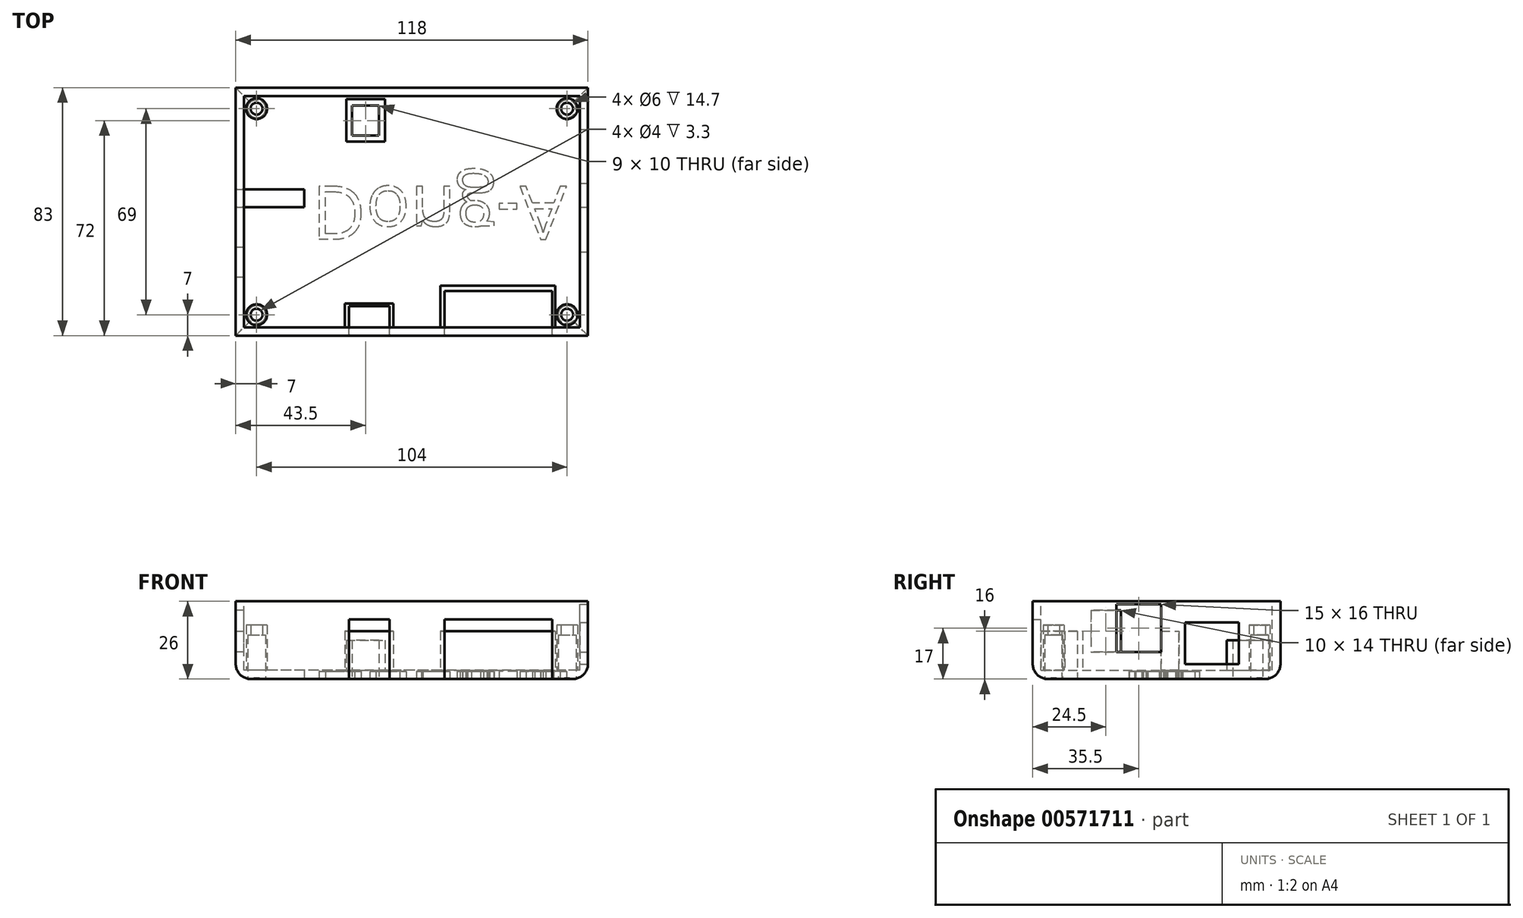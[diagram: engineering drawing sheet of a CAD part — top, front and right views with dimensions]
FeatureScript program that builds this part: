
annotation { "Feature Type Name" : "Feature", "Feature Type Description" : "" }
export const myFeature = defineFeature(function(context is Context, id is Id, definition is map)
    precondition{}
    {
        {
            var Q0;
            Q0=qCreatedBy(makeId("Top.planeOp"),FACE);
            var sketch = newSketch(context, id + "F0", { "sketchPlane" : qUnion([Q0])});
            skLineSegment(sketch, "E0.bottom", {"start": v(59, -41.5) * mm, "end": v(-59, -41.5) * mm});
            skLineSegment(sketch, "E0.top", {"start": v(59, 41.5) * mm, "end": v(-59, 41.5) * mm});
            skLineSegment(sketch, "E0.left", {"start": v(59, -41.5) * mm, "end": v(59, 41.5) * mm});
            skLineSegment(sketch, "E0.right", {"start": v(-59, -41.5) * mm, "end": v(-59, 41.5) * mm});
            skPoint(sketch, "E0.middle", {"position": v(0, 0) * mm});
            skSolve(sketch);
        }
        {
            var Q0;
            Q0=makeQuery(id+"F0.imprint","IMPRINT",FACE,{"disambiguationData":[TD([[makeQuery(id+"F0.imprint","IMPRINT",EDGE,{"derivedFrom":sQuery(id+"F0.wireOp",EDGE,"E0.bottom")}),-1.0]])]});
            extrude(context, id + "F1", {"entities" : qUnion([Q0]), "depth" : 26 * mm, "offsetDistance" : 25.4 * mm});
        }
        {
            var Q0;
            Q0=makeQuery(id+"F1.opExtrude","CAP_FACE",FACE,{"disambiguationData":[OSD([sQuery(id+"F0.wireOp",EDGE,"E0.bottom"),sQuery(id+"F0.wireOp",EDGE,"E0.top"),sQuery(id+"F0.wireOp",EDGE,"E0.left"),sQuery(id+"F0.wireOp",EDGE,"E0.right")])],"isStart":false});
            var sketch = newSketch(context, id + "F2", { "sketchPlane" : qUnion([Q0])});
            skLineSegment(sketch, "E1.bottom", {"start": v(56.25, -38.75) * mm, "end": v(-56.25, -38.75) * mm});
            skLineSegment(sketch, "E1.top", {"start": v(56.25, 38.75) * mm, "end": v(-56.25, 38.75) * mm});
            skLineSegment(sketch, "E1.left", {"start": v(56.25, -38.75) * mm, "end": v(56.25, 38.75) * mm});
            skLineSegment(sketch, "E1.right", {"start": v(-56.25, -38.75) * mm, "end": v(-56.25, 38.75) * mm});
            skPoint(sketch, "E1.middle", {"position": v(0, 0) * mm});
            skSolve(sketch);
        }
        {
            var Q0;
            Q0 = qSketchRegion(id + "F2", true);
            extrude(context, id + "F3", {"entities" : qUnion([Q0]), "operationType" : NewBodyOperationType.REMOVE, "oppositeDirection" : true, "depth" : 23 * mm, "offsetDistance" : 25.4 * mm});
        }
        {
            var Q0;
            Q0=makeQuery(id+"F1.opExtrude","CAP_FACE",FACE,{"disambiguationData":[OSD([sQuery(id+"F0.wireOp",EDGE,"E0.bottom"),sQuery(id+"F0.wireOp",EDGE,"E0.top"),sQuery(id+"F0.wireOp",EDGE,"E0.left"),sQuery(id+"F0.wireOp",EDGE,"E0.right")])],"isStart":true});
            var sketch = newSketch(context, id + "F4", { "sketchPlane" : qUnion([Q0])});
            skLineSegment(sketch, "E2.bottom", {"start": v(47, 41.5) * mm, "end": v(11, 41.5) * mm});
            skLineSegment(sketch, "E2.top", {"start": v(47, 26.5) * mm, "end": v(11, 26.5) * mm});
            skLineSegment(sketch, "E2.left", {"start": v(47, 41.5) * mm, "end": v(47, 26.5) * mm});
            skLineSegment(sketch, "E2.right", {"start": v(11, 41.5) * mm, "end": v(11, 26.5) * mm});
            skLineSegment(sketch, "E3.bottom", {"start": v(-7.5, 41.5) * mm, "end": v(-21, 41.5) * mm});
            skLineSegment(sketch, "E3.top", {"start": v(-7.5, 31.7) * mm, "end": v(-21, 31.7) * mm});
            skLineSegment(sketch, "E3.left", {"start": v(-7.5, 41.5) * mm, "end": v(-7.5, 31.7) * mm});
            skLineSegment(sketch, "E3.right", {"start": v(-21, 41.5) * mm, "end": v(-21, 31.7) * mm});
            skSolve(sketch);
        }
        {
            var Q0;
            Q0 = qSketchRegion(id + "F4", true);
            extrude(context, id + "F5", {"entities" : qUnion([Q0]), "operationType" : NewBodyOperationType.REMOVE, "oppositeDirection" : true, "depth" : 20 * mm, "offsetDistance" : 25.4 * mm});
        }
        {
            var Q0;
            Q0=makeQuery(id+"F3.boolean.opBoolean","COPY",FACE,{"derivedFrom":makeQuery(id+"F3.opExtrude","CAP_FACE",FACE,{"disambiguationData":[OSD([sQuery(id+"F2.wireOp",EDGE,"E1.bottom"),sQuery(id+"F2.wireOp",EDGE,"E1.top"),sQuery(id+"F2.wireOp",EDGE,"E1.left"),sQuery(id+"F2.wireOp",EDGE,"E1.right")])],"isStart":false})});
            var sketch = newSketch(context, id + "F6", { "sketchPlane" : qUnion([Q0])});
            skLineSegment(sketch, "E4.bottom", {"start": v(47, -38.75) * mm, "end": v(48, -38.75) * mm});
            skLineSegment(sketch, "E4.top", {"start": v(47, -24.75) * mm, "end": v(48, -24.75) * mm});
            skLineSegment(sketch, "E4.left", {"start": v(47, -38.75) * mm, "end": v(47, -24.75) * mm});
            skLineSegment(sketch, "E4.right", {"start": v(48, -38.75) * mm, "end": v(48, -24.75) * mm});
            skLineSegment(sketch, "E5.bottom", {"start": v(11, -38.75) * mm, "end": v(9.5, -38.75) * mm});
            skLineSegment(sketch, "E5.top", {"start": v(11, -24.75) * mm, "end": v(9.5, -24.75) * mm});
            skLineSegment(sketch, "E5.left", {"start": v(11, -38.75) * mm, "end": v(11, -24.75) * mm});
            skLineSegment(sketch, "E5.right", {"start": v(9.5, -38.75) * mm, "end": v(9.5, -24.75) * mm});
            skLineSegment(sketch, "E6.bottom", {"start": v(47, -24.75) * mm, "end": v(11, -24.75) * mm});
            skLineSegment(sketch, "E6.top", {"start": v(47, -26.5) * mm, "end": v(11, -26.5) * mm});
            skLineSegment(sketch, "E6.left", {"start": v(47, -24.75) * mm, "end": v(47, -26.5) * mm});
            skLineSegment(sketch, "E6.right", {"start": v(11, -24.75) * mm, "end": v(11, -26.5) * mm});
            skLineSegment(sketch, "E7.bottom", {"start": v(-7.5, -38.75) * mm, "end": v(-6.2, -38.75) * mm});
            skLineSegment(sketch, "E7.top", {"start": v(-7.5, -30.75) * mm, "end": v(-6.2, -30.75) * mm});
            skLineSegment(sketch, "E7.left", {"start": v(-7.5, -38.75) * mm, "end": v(-7.5, -30.75) * mm});
            skLineSegment(sketch, "E7.right", {"start": v(-6.2, -38.75) * mm, "end": v(-6.2, -30.75) * mm});
            skLineSegment(sketch, "E8.bottom", {"start": v(-21, -38.75) * mm, "end": v(-22.5, -38.75) * mm});
            skLineSegment(sketch, "E8.top", {"start": v(-21, -30.75) * mm, "end": v(-22.5, -30.75) * mm});
            skLineSegment(sketch, "E8.left", {"start": v(-21, -38.75) * mm, "end": v(-21, -30.75) * mm});
            skLineSegment(sketch, "E8.right", {"start": v(-22.5, -38.75) * mm, "end": v(-22.5, -30.75) * mm});
            skLineSegment(sketch, "E9.bottom", {"start": v(-7.5, -30.75) * mm, "end": v(-21, -30.75) * mm});
            skLineSegment(sketch, "E9.top", {"start": v(-7.5, -31.7) * mm, "end": v(-21, -31.7) * mm});
            skLineSegment(sketch, "E9.left", {"start": v(-7.5, -30.75) * mm, "end": v(-7.5, -31.7) * mm});
            skLineSegment(sketch, "E9.right", {"start": v(-21, -30.75) * mm, "end": v(-21, -31.7) * mm});
            skSolve(sketch);
        }
        {
            var Q0;
            Q0 = qSketchRegion(id + "F6", true);
            extrude(context, id + "F7", {"entities" : qUnion([Q0]), "operationType" : NewBodyOperationType.ADD, "depth" : 13 * mm, "offsetDistance" : 25.4 * mm});
        }
        {
            var Q0;
            Q0=makeQuery(id+"F1.opExtrude","SWEPT_FACE",FACE,{"disambiguationData":[OSD([sQuery(id+"F0.wireOp",EDGE,"E0.right")])]});
            var sketch = newSketch(context, id + "F8", { "sketchPlane" : qUnion([Q0])});
            skLineSegment(sketch, "E10.bottom", {"start": v(22, 23) * mm, "end": v(12, 23) * mm});
            skLineSegment(sketch, "E10.top", {"start": v(22, 9) * mm, "end": v(12, 9) * mm});
            skLineSegment(sketch, "E10.left", {"start": v(22, 23) * mm, "end": v(22, 9) * mm});
            skLineSegment(sketch, "E10.right", {"start": v(12, 23) * mm, "end": v(12, 9) * mm});
            skSolve(sketch);
        }
        {
            var Q0;
            Q0 = qSketchRegion(id + "F8", true);
            extrude(context, id + "F9", {"entities" : qUnion([Q0]), "operationType" : NewBodyOperationType.REMOVE, "oppositeDirection" : true, "depth" : 10 * mm, "offsetDistance" : 25.4 * mm});
        }
        {
            var Q0;
            Q0=makeQuery(id+"F1.opExtrude","CAP_FACE",FACE,{"disambiguationData":[OSD([sQuery(id+"F0.wireOp",EDGE,"E0.bottom"),sQuery(id+"F0.wireOp",EDGE,"E0.top"),sQuery(id+"F0.wireOp",EDGE,"E0.left"),sQuery(id+"F0.wireOp",EDGE,"E0.right")])],"isStart":true});
            var sketch = newSketch(context, id + "F10", { "sketchPlane" : qUnion([Q0])});
            skLineSegment(sketch, "E11.bottom", {"start": v(-59, -1.5) * mm, "end": v(-36, -1.5) * mm});
            skLineSegment(sketch, "E11.top", {"start": v(-59, -7.5) * mm, "end": v(-36, -7.5) * mm});
            skLineSegment(sketch, "E11.left", {"start": v(-59, -1.5) * mm, "end": v(-59, -7.5) * mm});
            skLineSegment(sketch, "E11.right", {"start": v(-36, -1.5) * mm, "end": v(-36, -7.5) * mm});
            skSolve(sketch);
        }
        {
            var Q0;
            Q0 = qSketchRegion(id + "F10", true);
            extrude(context, id + "F11", {"entities" : qUnion([Q0]), "operationType" : NewBodyOperationType.REMOVE, "oppositeDirection" : true, "depth" : 16 * mm, "offsetDistance" : 25.4 * mm});
        }
        {
            var Q0;
            Q0=makeQuery(id+"F1.opExtrude","CAP_FACE",FACE,{"disambiguationData":[OSD([sQuery(id+"F0.wireOp",EDGE,"E0.bottom"),sQuery(id+"F0.wireOp",EDGE,"E0.top"),sQuery(id+"F0.wireOp",EDGE,"E0.left"),sQuery(id+"F0.wireOp",EDGE,"E0.right")])],"isStart":true});
            var sketch = newSketch(context, id + "F12", { "sketchPlane" : qUnion([Q0])});
            skLineSegment(sketch, "E12.bottom", {"start": v(-20, -35.5) * mm, "end": v(-11, -35.5) * mm});
            skLineSegment(sketch, "E12.top", {"start": v(-20, -25.5) * mm, "end": v(-11, -25.5) * mm});
            skLineSegment(sketch, "E12.left", {"start": v(-20, -35.5) * mm, "end": v(-20, -25.5) * mm});
            skLineSegment(sketch, "E12.right", {"start": v(-11, -35.5) * mm, "end": v(-11, -25.5) * mm});
            skSolve(sketch);
        }
        {
            var Q0;
            Q0 = qSketchRegion(id + "F12", true);
            extrude(context, id + "F13", {"entities" : qUnion([Q0]), "operationType" : NewBodyOperationType.REMOVE, "oppositeDirection" : true, "depth" : 10 * mm, "offsetDistance" : 25.4 * mm});
        }
        {
            var Q0;
            Q0=makeQuery(id+"F1.opExtrude","SWEPT_FACE",FACE,{"disambiguationData":[OSD([sQuery(id+"F0.wireOp",EDGE,"E0.left")])]});
            var sketch = newSketch(context, id + "F14", { "sketchPlane" : qUnion([Q0])});
            skLineSegment(sketch, "E13.bottom", {"start": v(27.5, 19) * mm, "end": v(9.5, 19) * mm});
            skLineSegment(sketch, "E13.top", {"start": v(27.5, 5) * mm, "end": v(9.5, 5) * mm});
            skLineSegment(sketch, "E13.left", {"start": v(27.5, 19) * mm, "end": v(27.5, 5) * mm});
            skLineSegment(sketch, "E13.right", {"start": v(9.5, 19) * mm, "end": v(9.5, 5) * mm});
            skLineSegment(sketch, "E14.bottom", {"start": v(-13.5, 9) * mm, "end": v(1.5, 9) * mm});
            skLineSegment(sketch, "E14.top", {"start": v(-13.5, 25) * mm, "end": v(1.5, 25) * mm});
            skLineSegment(sketch, "E14.left", {"start": v(-13.5, 9) * mm, "end": v(-13.5, 25) * mm});
            skLineSegment(sketch, "E14.right", {"start": v(1.5, 9) * mm, "end": v(1.5, 25) * mm});
            skSolve(sketch);
        }
        {
            var Q0;
            Q0 = qSketchRegion(id + "F14", true);
            extrude(context, id + "F15", {"entities" : qUnion([Q0]), "operationType" : NewBodyOperationType.REMOVE, "oppositeDirection" : true, "depth" : 10 * mm, "offsetDistance" : 25.4 * mm});
        }
        {
            var Q0;
            Q0=makeQuery(id+"F3.boolean.opBoolean","COPY",FACE,{"derivedFrom":makeQuery(id+"F3.opExtrude","CAP_FACE",FACE,{"disambiguationData":[OSD([sQuery(id+"F2.wireOp",EDGE,"E1.bottom"),sQuery(id+"F2.wireOp",EDGE,"E1.top"),sQuery(id+"F2.wireOp",EDGE,"E1.left"),sQuery(id+"F2.wireOp",EDGE,"E1.right")])],"isStart":false})});
            var sketch = newSketch(context, id + "F16", { "sketchPlane" : qUnion([Q0])});
            skLineSegment(sketch, "E15.bottom", {"start": v(-22, 25.5) * mm, "end": v(-11, 25.5) * mm});
            skLineSegment(sketch, "E15.top", {"start": v(-22, 23.5) * mm, "end": v(-11, 23.5) * mm});
            skLineSegment(sketch, "E15.left", {"start": v(-22, 25.5) * mm, "end": v(-22, 23.5) * mm});
            skLineSegment(sketch, "E15.right", {"start": v(-11, 25.5) * mm, "end": v(-11, 23.5) * mm});
            skLineSegment(sketch, "E16.bottom", {"start": v(-11, 23.5) * mm, "end": v(-9, 23.5) * mm});
            skLineSegment(sketch, "E16.top", {"start": v(-11, 37.68) * mm, "end": v(-9, 37.68) * mm});
            skLineSegment(sketch, "E16.left", {"start": v(-11, 23.5) * mm, "end": v(-11, 37.68) * mm});
            skLineSegment(sketch, "E16.right", {"start": v(-9, 23.5) * mm, "end": v(-9, 37.68) * mm});
            skLineSegment(sketch, "E17.bottom", {"start": v(-22, 25.5) * mm, "end": v(-20, 25.5) * mm});
            skLineSegment(sketch, "E17.top", {"start": v(-22, 37.68) * mm, "end": v(-20, 37.68) * mm});
            skLineSegment(sketch, "E17.left", {"start": v(-22, 25.5) * mm, "end": v(-22, 37.68) * mm});
            skLineSegment(sketch, "E17.right", {"start": v(-20, 25.5) * mm, "end": v(-20, 37.68) * mm});
            skLineSegment(sketch, "E18.bottom", {"start": v(-20, 37.68) * mm, "end": v(-11, 37.68) * mm});
            skLineSegment(sketch, "E18.top", {"start": v(-20, 35.5) * mm, "end": v(-11, 35.5) * mm});
            skLineSegment(sketch, "E18.left", {"start": v(-20, 37.68) * mm, "end": v(-20, 35.5) * mm});
            skLineSegment(sketch, "E18.right", {"start": v(-11, 37.68) * mm, "end": v(-11, 35.5) * mm});
            skSolve(sketch);
        }
        {
            var Q0;
            Q0 = qSketchRegion(id + "F16", true);
            extrude(context, id + "F17", {"entities" : qUnion([Q0]), "operationType" : NewBodyOperationType.ADD, "depth" : 10 * mm, "offsetDistance" : 25.4 * mm});
        }
        {
            var Q0;
            Q0=makeQuery(id+"F1.opExtrude","CAP_FACE",FACE,{"disambiguationData":[OSD([sQuery(id+"F0.wireOp",EDGE,"E0.bottom"),sQuery(id+"F0.wireOp",EDGE,"E0.top"),sQuery(id+"F0.wireOp",EDGE,"E0.left"),sQuery(id+"F0.wireOp",EDGE,"E0.right")])],"isStart":true});
            var sketch = newSketch(context, id + "F18", { "sketchPlane" : qUnion([Q0])});
            skCircle(sketch, "E19", {"center": v(-52, -34.5) * mm, "radius": 3 * mm});
            skCircle(sketch, "E20", {"center": v(-52, 34.5) * mm, "radius": 3 * mm});
            skCircle(sketch, "E21", {"center": v(52, -34.5) * mm, "radius": 3 * mm});
            skCircle(sketch, "E22", {"center": v(52, 34.5) * mm, "radius": 3 * mm});
            skSolve(sketch);
        }
        {
            var Q0;
            Q0 = qSketchRegion(id + "F18", true);
            extrude(context, id + "F19", {"entities" : qUnion([Q0]), "operationType" : NewBodyOperationType.REMOVE, "oppositeDirection" : true, "depth" : 25.4 * mm, "offsetDistance" : 25.4 * mm});
        }
        {
            var Q0;
            {var subQ0=sQuery(id+"F2.wireOp",EDGE,"E1.bottom");var subQ1=sQuery(id+"F2.wireOp",EDGE,"E1.top");var subQ2=sQuery(id+"F2.wireOp",EDGE,"E1.left");var subQ3=sQuery(id+"F2.wireOp",EDGE,"E1.right");Q0=makeQuery(id+"F19.boolean.opBoolean","SPLIT",FACE,{"disambiguationData":[TD([makeQuery(id+"F3.boolean.opBoolean","COPY",FACE,{"derivedFrom":makeQuery(id+"F3.opExtrude","SWEPT_FACE",FACE,{"disambiguationData":[OSD([subQ0])]})}),makeQuery(id+"F3.boolean.opBoolean","COPY",FACE,{"derivedFrom":makeQuery(id+"F3.opExtrude","SWEPT_FACE",FACE,{"disambiguationData":[OSD([subQ1])]})}),makeQuery(id+"F3.boolean.opBoolean","COPY",FACE,{"derivedFrom":makeQuery(id+"F3.opExtrude","SWEPT_FACE",FACE,{"disambiguationData":[OSD([subQ2])]})}),makeQuery(id+"F3.boolean.opBoolean","COPY",FACE,{"derivedFrom":makeQuery(id+"F3.opExtrude","SWEPT_FACE",FACE,{"disambiguationData":[OSD([subQ3])]})}),makeQuery(id+"F7.opExtrude","SWEPT_FACE",FACE,{"disambiguationData":[OSD([sQuery(id+"F6.wireOp",EDGE,"E4.top"),sQuery(id+"F6.wireOp",EDGE,"E5.top"),sQuery(id+"F6.wireOp",EDGE,"E6.bottom")])]}),makeQuery(id+"F7.opExtrude","SWEPT_FACE",FACE,{"disambiguationData":[OSD([sQuery(id+"F6.wireOp",EDGE,"E4.right")])]}),makeQuery(id+"F7.opExtrude","SWEPT_FACE",FACE,{"disambiguationData":[OSD([sQuery(id+"F6.wireOp",EDGE,"E5.right")])]}),makeQuery(id+"F7.opExtrude","SWEPT_FACE",FACE,{"disambiguationData":[OSD([sQuery(id+"F6.wireOp",EDGE,"E7.top"),sQuery(id+"F6.wireOp",EDGE,"E8.top"),sQuery(id+"F6.wireOp",EDGE,"E9.bottom")])]}),makeQuery(id+"F7.opExtrude","SWEPT_FACE",FACE,{"disambiguationData":[OSD([sQuery(id+"F6.wireOp",EDGE,"E7.right")])]}),makeQuery(id+"F7.opExtrude","SWEPT_FACE",FACE,{"disambiguationData":[OSD([sQuery(id+"F6.wireOp",EDGE,"E8.right")])]}),makeQuery(id+"F11.boolean.opBoolean","COPY",FACE,{"derivedFrom":makeQuery(id+"F11.opExtrude","SWEPT_FACE",FACE,{"disambiguationData":[OSD([sQuery(id+"F10.wireOp",EDGE,"E11.bottom")])]})}),makeQuery(id+"F11.boolean.opBoolean","COPY",FACE,{"derivedFrom":makeQuery(id+"F11.opExtrude","SWEPT_FACE",FACE,{"disambiguationData":[OSD([sQuery(id+"F10.wireOp",EDGE,"E11.top")])]})}),makeQuery(id+"F11.boolean.opBoolean","COPY",FACE,{"derivedFrom":makeQuery(id+"F11.opExtrude","SWEPT_FACE",FACE,{"disambiguationData":[OSD([sQuery(id+"F10.wireOp",EDGE,"E11.right")])]})}),makeQuery(id+"F17.opExtrude","SWEPT_FACE",FACE,{"disambiguationData":[OSD([sQuery(id+"F16.wireOp",EDGE,"E15.top"),sQuery(id+"F16.wireOp",EDGE,"E16.bottom")])]}),makeQuery(id+"F17.opExtrude","SWEPT_FACE",FACE,{"disambiguationData":[OSD([sQuery(id+"F16.wireOp",EDGE,"E15.left"),sQuery(id+"F16.wireOp",EDGE,"E17.left")])]}),makeQuery(id+"F17.opExtrude","SWEPT_FACE",FACE,{"disambiguationData":[OSD([sQuery(id+"F16.wireOp",EDGE,"E16.top"),sQuery(id+"F16.wireOp",EDGE,"E17.top"),sQuery(id+"F16.wireOp",EDGE,"E18.bottom")])]}),makeQuery(id+"F17.opExtrude","SWEPT_FACE",FACE,{"disambiguationData":[OSD([sQuery(id+"F16.wireOp",EDGE,"E16.right")])]}),makeQuery(id+"F19.opExtrude","SWEPT_FACE",FACE,{"disambiguationData":[OSD([sQuery(id+"F18.wireOp",EDGE,"E19")])]}),makeQuery(id+"F19.opExtrude","SWEPT_FACE",FACE,{"disambiguationData":[OSD([sQuery(id+"F18.wireOp",EDGE,"E20")])]}),makeQuery(id+"F19.opExtrude","SWEPT_FACE",FACE,{"disambiguationData":[OSD([sQuery(id+"F18.wireOp",EDGE,"E21")])]}),makeQuery(id+"F19.opExtrude","SWEPT_FACE",FACE,{"disambiguationData":[OSD([sQuery(id+"F18.wireOp",EDGE,"E22")])]})])],"derivedFrom":makeQuery(id+"F3.boolean.opBoolean","COPY",FACE,{"derivedFrom":makeQuery(id+"F3.opExtrude","CAP_FACE",FACE,{"disambiguationData":[OSD([subQ0,subQ1,subQ2,subQ3])],"isStart":false})})});}
            var sketch = newSketch(context, id + "F20", { "sketchPlane" : qUnion([Q0])});
            skCircle(sketch, "E23", {"center": v(-52, 34.5) * mm, "radius": 3.5 * mm});
            skCircle(sketch, "E24", {"center": v(-52, -34.5) * mm, "radius": 3.5 * mm});
            skCircle(sketch, "E25", {"center": v(52, -34.5) * mm, "radius": 3.5 * mm});
            skCircle(sketch, "E26", {"center": v(52, 34.5) * mm, "radius": 3.5 * mm});
            skSolve(sketch);
        }
        {
            var Q0;
            Q0=makeQuery(id+"F1.opExtrude","CAP_FACE",FACE,{"disambiguationData":[OSD([sQuery(id+"F0.wireOp",EDGE,"E0.bottom"),sQuery(id+"F0.wireOp",EDGE,"E0.top"),sQuery(id+"F0.wireOp",EDGE,"E0.left"),sQuery(id+"F0.wireOp",EDGE,"E0.right")])],"isStart":true});
            var sketch = newSketch(context, id + "F21", { "sketchPlane" : qUnion([Q0])});
            skCircle(sketch, "E27", {"center": v(52, -34.5) * mm, "radius": 3 * mm});
            skCircle(sketch, "E28", {"center": v(-52, -34.5) * mm, "radius": 3 * mm});
            skCircle(sketch, "E29", {"center": v(52, 34.5) * mm, "radius": 3 * mm});
            skCircle(sketch, "E30", {"center": v(-52, 34.5) * mm, "radius": 3 * mm});
            skSolve(sketch);
        }
        {
            var Q0;
            Q0=makeQuery(id+"F1.opExtrude","CAP_FACE",FACE,{"disambiguationData":[OSD([sQuery(id+"F0.wireOp",EDGE,"E0.bottom"),sQuery(id+"F0.wireOp",EDGE,"E0.top"),sQuery(id+"F0.wireOp",EDGE,"E0.left"),sQuery(id+"F0.wireOp",EDGE,"E0.right")])],"isStart":true});
            var sketch = newSketch(context, id + "F22", { "sketchPlane" : qUnion([Q0])});
            skCircle(sketch, "E31", {"center": v(-52, 34.5) * mm, "radius": 2 * mm});
            skCircle(sketch, "E32", {"center": v(52, 34.5) * mm, "radius": 2 * mm});
            skCircle(sketch, "E33", {"center": v(52, -34.5) * mm, "radius": 2 * mm});
            skCircle(sketch, "E34", {"center": v(-52, -34.5) * mm, "radius": 2 * mm});
            skSolve(sketch);
        }
        {
            var Q0;
            Q0 = qSketchRegion(id + "F20", true);
            extrude(context, id + "F23", {"entities" : qUnion([Q0]), "operationType" : NewBodyOperationType.ADD, "depth" : 15 * mm, "offsetDistance" : 25.4 * mm});
        }
        {
            var Q0;
            Q0 = qSketchRegion(id + "F21", true);
            extrude(context, id + "F24", {"entities" : qUnion([Q0]), "operationType" : NewBodyOperationType.REMOVE, "oppositeDirection" : true, "depth" : 14.7 * mm, "offsetDistance" : 25.4 * mm});
        }
        {
            var Q0;
            Q0 = qSketchRegion(id + "F22", true);
            extrude(context, id + "F25", {"entities" : qUnion([Q0]), "operationType" : NewBodyOperationType.REMOVE, "oppositeDirection" : true, "depth" : 25.4 * mm, "offsetDistance" : 25.4 * mm});
        }
        {
            var Q0;
            Q0=makeQuery(id+"F1.opExtrude","CAP_FACE",FACE,{"disambiguationData":[OSD([sQuery(id+"F0.wireOp",EDGE,"E0.bottom"),sQuery(id+"F0.wireOp",EDGE,"E0.top"),sQuery(id+"F0.wireOp",EDGE,"E0.left"),sQuery(id+"F0.wireOp",EDGE,"E0.right")])],"isStart":true});
            var sketch = newSketch(context, id + "F26", { "sketchPlane" : qUnion([Q0])});
            skText(sketch, "E35", { "text": "Dong-A", "fontName": "OpenSans-Regular.ttf"});
            const initialGuessF26  = {"E35": [-0.03347, -0.00847, 1, 0, 0.0178]};
            skSetInitialGuess(sketch, initialGuessF26);
            skSolve(sketch);
        }
        {
            var Q0;
            Q0 = qSketchRegion(id + "F26", true);
            extrude(context, id + "F27", {"entities" : qUnion([Q0]), "operationType" : NewBodyOperationType.REMOVE, "oppositeDirection" : true, "depth" : 2.54 * mm, "offsetDistance" : 25.4 * mm});
        }
        {
            var Q0;
            {var subQ0=sQuery(id+"F0.wireOp",EDGE,"E0.bottom");var subQ1=sQuery(id+"F0.wireOp",EDGE,"E0.right");Q0=makeQuery(id+"F5.boolean.opBoolean","SPLIT",EDGE,{"disambiguationData":[TD([makeQuery(id+"F1.opExtrude","SWEPT_FACE",FACE,{"disambiguationData":[OSD([subQ1])]})])],"derivedFrom":makeQuery(id+"F1.opExtrude","CAP_EDGE",EDGE,{"disambiguationData":[OSD([subQ0])],"isStart":true})});}
            var Q1;
            {var subQ0=sQuery(id+"F0.wireOp",EDGE,"E0.bottom");Q1=makeQuery(id+"F5.boolean.opBoolean","SPLIT",EDGE,{"disambiguationData":[TD([makeQuery(id+"F5.opExtrude","SWEPT_FACE",FACE,{"disambiguationData":[OSD([sQuery(id+"F4.wireOp",EDGE,"E2.right")])]})])],"derivedFrom":makeQuery(id+"F1.opExtrude","CAP_EDGE",EDGE,{"disambiguationData":[OSD([subQ0])],"isStart":true})});}
            var Q2;
            {var subQ0=sQuery(id+"F0.wireOp",EDGE,"E0.bottom");var subQ1=sQuery(id+"F0.wireOp",EDGE,"E0.left");Q2=makeQuery(id+"F5.boolean.opBoolean","SPLIT",EDGE,{"disambiguationData":[TD([makeQuery(id+"F1.opExtrude","SWEPT_FACE",FACE,{"disambiguationData":[OSD([subQ1])]})])],"derivedFrom":makeQuery(id+"F1.opExtrude","CAP_EDGE",EDGE,{"disambiguationData":[OSD([subQ0])],"isStart":true})});}
            var Q3;
            Q3=makeQuery(id+"F1.opExtrude","CAP_EDGE",EDGE,{"disambiguationData":[OSD([sQuery(id+"F0.wireOp",EDGE,"E0.left")])],"isStart":true});
            var Q4;
            Q4=makeQuery(id+"F1.opExtrude","CAP_EDGE",EDGE,{"disambiguationData":[OSD([sQuery(id+"F0.wireOp",EDGE,"E0.top")])],"isStart":true});
            var Q5;
            {var subQ0=sQuery(id+"F0.wireOp",EDGE,"E0.right");var subQ1=sQuery(id+"F0.wireOp",EDGE,"E0.top");Q5=makeQuery(id+"F11.boolean.opBoolean","SPLIT",EDGE,{"disambiguationData":[TD([makeQuery(id+"F1.opExtrude","SWEPT_FACE",FACE,{"disambiguationData":[OSD([subQ1])]})])],"derivedFrom":makeQuery(id+"F1.opExtrude","CAP_EDGE",EDGE,{"disambiguationData":[OSD([subQ0])],"isStart":true})});}
            var Q6;
            {var subQ0=sQuery(id+"F0.wireOp",EDGE,"E0.bottom");var subQ1=sQuery(id+"F0.wireOp",EDGE,"E0.right");Q6=makeQuery(id+"F11.boolean.opBoolean","SPLIT",EDGE,{"disambiguationData":[TD([makeQuery(id+"F1.opExtrude","SWEPT_FACE",FACE,{"disambiguationData":[OSD([subQ0])]})])],"derivedFrom":makeQuery(id+"F1.opExtrude","CAP_EDGE",EDGE,{"disambiguationData":[OSD([subQ1])],"isStart":true})});}
            fillet(context, id + "F28", {"entities" : qUnion([Q0, Q1, Q2, Q3, Q4, Q5, Q6]), "radius" : 5.08 * mm, "tangentPropagation" : true, "allowEdgeOverflow" : false});
        }
    });
